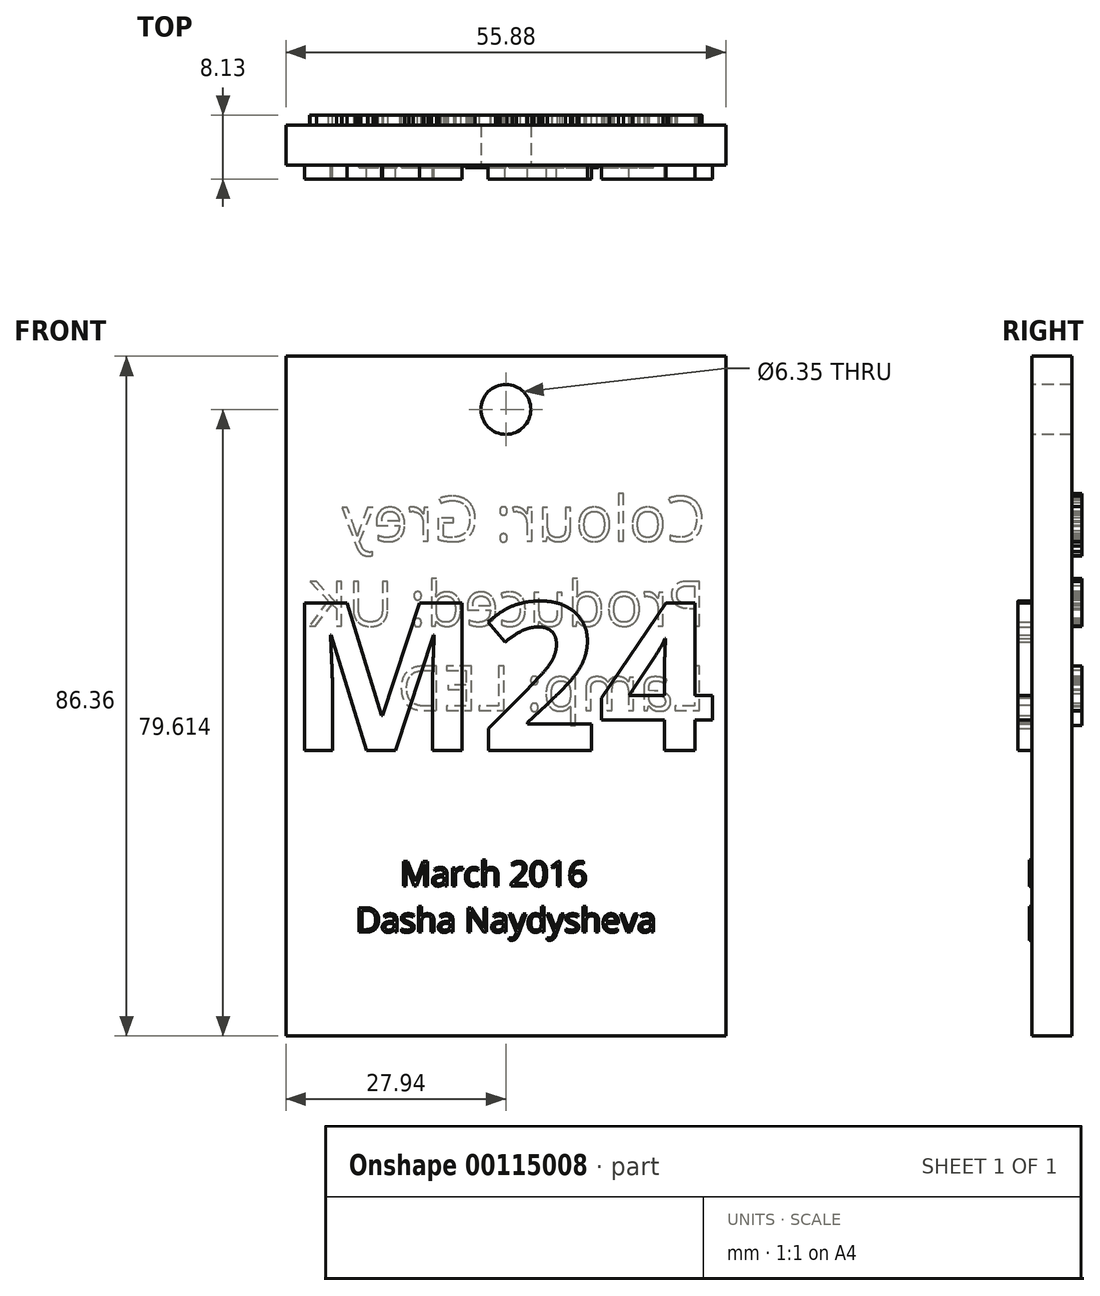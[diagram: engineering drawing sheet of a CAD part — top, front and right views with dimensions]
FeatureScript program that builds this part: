
annotation { "Feature Type Name" : "Feature", "Feature Type Description" : "" }
export const myFeature = defineFeature(function(context is Context, id is Id, definition is map)
    precondition{}
    {
        {
            var Q0;
            Q0=qCreatedBy(makeId("Front.planeOp"),FACE);
            var sketch = newSketch(context, id + "F0", { "sketchPlane" : qUnion([Q0])});
            skLineSegment(sketch, "E0", {"start": v(0, 43.18) * mm, "end": v(-27.94, 43.18) * mm});
            skLineSegment(sketch, "E1", {"start": v(-27.94, 43.18) * mm, "end": v(-27.94, 0) * mm});
            skLineSegment(sketch, "E2", {"start": v(-27.94, 0) * mm, "end": v(-27.94, -43.18) * mm});
            skLineSegment(sketch, "E3", {"start": v(-27.94, -43.18) * mm, "end": v(0, -43.18) * mm});
            skLineSegment(sketch, "E4", {"start": v(0, -43.18) * mm, "end": v(27.94, -43.18) * mm});
            skLineSegment(sketch, "E5", {"start": v(27.94, -43.18) * mm, "end": v(27.94, 0) * mm});
            skLineSegment(sketch, "E6", {"start": v(27.94, 0) * mm, "end": v(27.94, 43.18) * mm});
            skLineSegment(sketch, "E7", {"start": v(27.94, 43.18) * mm, "end": v(0, 43.18) * mm});
            skSolve(sketch);
        }
        {
            var Q0;
            Q0=makeQuery(id+"F0.imprint","IMPRINT",FACE,{"disambiguationData":[TD([[makeQuery(id+"F0.imprint","IMPRINT",EDGE,{"derivedFrom":sQuery(id+"F0.wireOp",EDGE,"E0")}),1.0]])]});
            extrude(context, id + "F1", {"entities" : qUnion([Q0]), "depth" : 5.08 * mm});
        }
        {
            var Q0;
            Q0=makeQuery(id+"F1.opExtrude","CAP_FACE",FACE,{"disambiguationData":[OSD([sQuery(id+"F0.wireOp",EDGE,"E0"),sQuery(id+"F0.wireOp",EDGE,"E1"),sQuery(id+"F0.wireOp",EDGE,"E2"),sQuery(id+"F0.wireOp",EDGE,"E3"),sQuery(id+"F0.wireOp",EDGE,"E4"),sQuery(id+"F0.wireOp",EDGE,"E5"),sQuery(id+"F0.wireOp",EDGE,"E6"),sQuery(id+"F0.wireOp",EDGE,"E7")])],"isStart":false});
            var sketch = newSketch(context, id + "F2", { "sketchPlane" : qUnion([Q0])});
            skText(sketch, "E8", { "text": "M24", "fontName": "OpenSans-Bold.ttf"});
            const initialGuessF2  = {"E8": [-0.02794, -0.00687, 1, 0, 0.01886]};
            skSetInitialGuess(sketch, initialGuessF2);
            skSolve(sketch);
        }
        {
            var Q0;
            Q0 = qSketchRegion(id + "F2", true);
            extrude(context, id + "F3", {"entities" : qUnion([Q0]), "operationType" : NewBodyOperationType.ADD, "depth" : 1.78 * mm});
        }
        {
            var Q0;
            {var subQ0=sQuery(id+"F0.wireOp",EDGE,"E7");var subQ1=sQuery(id+"F0.wireOp",EDGE,"E0");var subQ2=sQuery(id+"F0.wireOp",EDGE,"E2");var subQ3=sQuery(id+"F0.wireOp",EDGE,"E1");var subQ4=sQuery(id+"F0.wireOp",EDGE,"E6");var subQ5=sQuery(id+"F0.wireOp",EDGE,"E5");var subQ6=sQuery(id+"F0.wireOp",EDGE,"E4");var subQ7=sQuery(id+"F0.wireOp",EDGE,"E3");Q0=makeQuery(id+"F3.boolean.opBoolean","SPLIT",FACE,{"disambiguationData":[TD([makeQuery(id+"F3.opExtrude","SWEPT_FACE",FACE,{"disambiguationData":[OSD([sQuery(id+"F2.wireOp",EDGE,"E8.sketch_text.stroke-0")])]})])],"derivedFrom":makeQuery(id+"F1.opExtrude","CAP_FACE",FACE,{"disambiguationData":[OSD([subQ1,subQ3,subQ2,subQ7,subQ6,subQ5,subQ4,subQ0])],"isStart":false})});}
            var sketch = newSketch(context, id + "F4", { "sketchPlane" : qUnion([Q0])});
            skText(sketch, "E9", { "text": "     March 2016\nDasha Naydysheva", "fontName": "OpenSans-Regular.ttf"});
            const initialGuessF4  = {"E9": [-0.01905, -0.0241, 1, 0, 0.00311]};
            skSetInitialGuess(sketch, initialGuessF4);
            skSolve(sketch);
        }
        {
            var Q0;
            Q0=makeQuery(id+"F1.opExtrude","CAP_FACE",FACE,{"disambiguationData":[OSD([sQuery(id+"F0.wireOp",EDGE,"E0"),sQuery(id+"F0.wireOp",EDGE,"E1"),sQuery(id+"F0.wireOp",EDGE,"E2"),sQuery(id+"F0.wireOp",EDGE,"E3"),sQuery(id+"F0.wireOp",EDGE,"E4"),sQuery(id+"F0.wireOp",EDGE,"E5"),sQuery(id+"F0.wireOp",EDGE,"E6"),sQuery(id+"F0.wireOp",EDGE,"E7")])],"isStart":true});
            var sketch = newSketch(context, id + "F5", { "sketchPlane" : qUnion([Q0])});
            skText(sketch, "E10", { "text": "Colour: Grey\nProduced: UK\nLamp: LED", "fontName": "OpenSans-Regular.ttf"});
            const initialGuessF5  = {"E10": [-0.0254, 0.0197, 1, 0, 0.0057]};
            skSetInitialGuess(sketch, initialGuessF5);
            skSolve(sketch);
        }
        {
            var Q0;
            Q0 = qSketchRegion(id + "F5", true);
            extrude(context, id + "F6", {"entities" : qUnion([Q0]), "operationType" : NewBodyOperationType.ADD, "depth" : 1.27 * mm});
        }
        {
            var Q0;
            Q0=makeQuery(id+"F4.imprint","IMPRINT",FACE,{"disambiguationData":[TD([[makeQuery(id+"F4.imprint","IMPRINT",EDGE,{"derivedFrom":sQuery(id+"F4.wireOp",EDGE,"E9.sketch_text.stroke-0")}),1.0]])]});
            var sketch = newSketch(context, id + "F7", { "sketchPlane" : qUnion([Q0])});
            skCircle(sketch, "E11", {"center": v(0, 36.43) * mm, "radius": 4.46 * mm});
            skSolve(sketch);
        }
        {
            var Q0;
            Q0=sQuery(id+"F7.wireOp",VERTEX,"E11.center");
            var Q1;
            Q1=makeQuery(id+"F1.opExtrude","SWEPT_BODY",BODY,{"disambiguationData":[OSD([sQuery(id+"F0.wireOp",EDGE,"E0"),sQuery(id+"F0.wireOp",EDGE,"E1"),sQuery(id+"F0.wireOp",EDGE,"E2"),sQuery(id+"F0.wireOp",EDGE,"E3"),sQuery(id+"F0.wireOp",EDGE,"E4"),sQuery(id+"F0.wireOp",EDGE,"E5"),sQuery(id+"F0.wireOp",EDGE,"E6"),sQuery(id+"F0.wireOp",EDGE,"E7")])]});
            hole(context, id + "F8", {"style" : HoleStyle.SIMPLE, "endStyle" : HoleEndStyle.THROUGH, "holeDiameter" : 6.35 * mm, "locations" : qUnion([Q0]), "scope" : qUnion([Q1]), "isTappedThrough" : true});
        }
        {
            var Q0;
            Q0 = qSketchRegion(id + "F4", true);
            extrude(context, id + "F9", {"entities" : qUnion([Q0]), "operationType" : NewBodyOperationType.ADD, "depth" : 0.3 * mm});
        }
    });
